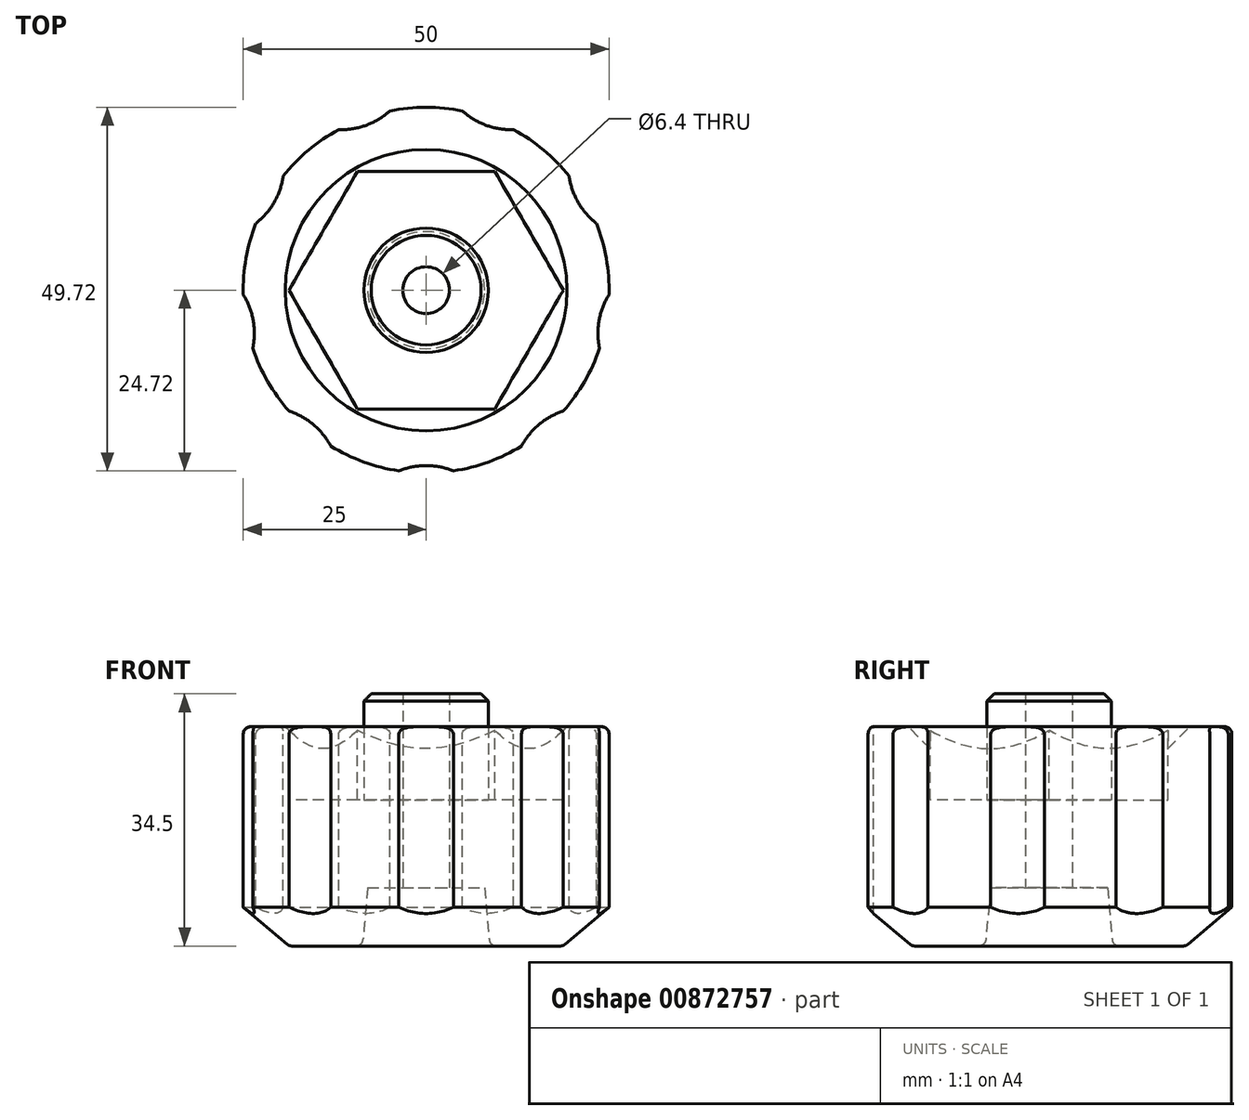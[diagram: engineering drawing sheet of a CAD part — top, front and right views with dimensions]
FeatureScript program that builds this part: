
annotation { "Feature Type Name" : "Feature", "Feature Type Description" : "" }
export const myFeature = defineFeature(function(context is Context, id is Id, definition is map)
    precondition{}
    {
        {
            var Q0;
            Q0=qCreatedBy(makeId("Front.planeOp"),FACE);
            var sketch = newSketch(context, id + "F0", { "sketchPlane" : qUnion([Q0])});
            skLineSegment(sketch, "E0", {"start": v(0, -6.14) * mm, "end": v(0, 36.57) * mm, "construction": true});
            skLineSegment(sketch, "E1", {"start": v(8.7, 0) * mm, "end": v(18.7, 0) * mm});
            skLineSegment(sketch, "E2", {"start": v(18.7, 0) * mm, "end": v(25, 5.29) * mm});
            skLineSegment(sketch, "E3", {"start": v(25, 5.29) * mm, "end": v(25, 30) * mm});
            skLineSegment(sketch, "E4", {"start": v(25, 30) * mm, "end": v(19.25, 30) * mm});
            skLineSegment(sketch, "E5", {"start": v(3.2, 34.5) * mm, "end": v(3.2, 8) * mm});
            skLineSegment(sketch, "E6", {"start": v(3.2, 8) * mm, "end": v(8, 8) * mm});
            skLineSegment(sketch, "E7", {"start": v(8, 8) * mm, "end": v(8.7, 0) * mm});
            skLineSegment(sketch, "E8", {"start": v(-29.63, 0) * mm, "end": v(44.02, 0) * mm, "construction": true});
            skLineSegment(sketch, "E9", {"start": v(19.25, 30) * mm, "end": v(16.25, 27) * mm});
            skLineSegment(sketch, "E10", {"start": v(16.25, 27) * mm, "end": v(16.25, 20) * mm});
            skLineSegment(sketch, "E11", {"start": v(16.25, 20) * mm, "end": v(8.5, 20) * mm});
            skLineSegment(sketch, "E12", {"start": v(8.5, 20) * mm, "end": v(8.5, 33.5) * mm});
            skLineSegment(sketch, "E13", {"start": v(8.5, 33.5) * mm, "end": v(7.5, 34.5) * mm});
            skLineSegment(sketch, "E14", {"start": v(7.5, 34.5) * mm, "end": v(3.2, 34.5) * mm});
            skSolve(sketch);
        }
        {
            var Q0;
            Q0=makeQuery(id+"F0.imprint","IMPRINT",FACE,{"disambiguationData":[TD([[makeQuery(id+"F0.imprint","IMPRINT",EDGE,{"derivedFrom":sQuery(id+"F0.wireOp",EDGE,"E1")}),1.0]])]});
            var Q1;
            Q1=sQuery(id+"F0.wireOp",EDGE,"E0");
            revolve(context, id + "F1", {"surfaceOperationType" : NewSurfaceOperationType.NEW, "entities" : qUnion([Q0]), "axis" : qUnion([Q1]), "revolveType" : RevolveType.FULL});
        }
        {
            var Q0;
            Q0=makeQuery(id+"F1.opRevolve","SWEPT_FACE",FACE,{"disambiguationData":[OSD([sQuery(id+"F0.wireOp",EDGE,"E4")])]});
            var sketch = newSketch(context, id + "F2", { "sketchPlane" : qUnion([Q0])});
            skLineSegment(sketch, "E15", {"start": v(0, 0) * mm, "end": v(0, 71.94) * mm, "construction": true});
            skLineSegment(sketch, "E16", {"start": v(0, 0) * mm, "end": v(26.2, 71.99) * mm, "construction": true});
            skCircle(sketch, "E17", {"center": v(11.63, 31.95) * mm, "radius": 10 * mm});
            skCircle(sketch, "E18.1.0", {"center": v(-11.63, 31.95) * mm, "radius": 10 * mm});
            skCircle(sketch, "E18.2.0", {"center": v(-29.44, 17) * mm, "radius": 10 * mm});
            skCircle(sketch, "E18.3.0", {"center": v(-33.48, -5.9) * mm, "radius": 10 * mm});
            skCircle(sketch, "E18.4.0", {"center": v(-21.85, -26.05) * mm, "radius": 10 * mm});
            skCircle(sketch, "E18.5.0", {"center": v(0, -34) * mm, "radius": 10 * mm});
            skCircle(sketch, "E18.6.0", {"center": v(21.85, -26.05) * mm, "radius": 10 * mm});
            skCircle(sketch, "E18.7.0", {"center": v(33.48, -5.9) * mm, "radius": 10 * mm});
            skCircle(sketch, "E18.8.0", {"center": v(29.44, 17) * mm, "radius": 10 * mm});
            skPoint(sketch, "E18.center", {"position": v(0, 0) * mm});
            skSolve(sketch);
        }
        {
            var Q0;
            Q0 = qSketchRegion(id + "F2", true);
            extrude(context, id + "F3", {"entities" : qUnion([Q0]), "operationType" : NewBodyOperationType.REMOVE, "endBound" : BoundingType.THROUGH_ALL, "oppositeDirection" : true, "depth" : 25 * mm, "offsetDistance" : 25 * mm});
        }
        {
            var Q0;
            Q0=makeQuery(id+"F1.opRevolve","SWEPT_EDGE",EDGE,{"disambiguationData":[OSD([sQuery(id+"F0.wireOp",EDGE,"E1"),sQuery(id+"F0.wireOp",EDGE,"E7")])]});
            var Q1;
            Q1=makeQuery(id+"F1.opRevolve","SWEPT_EDGE",EDGE,{"disambiguationData":[OSD([sQuery(id+"F0.wireOp",EDGE,"E1"),sQuery(id+"F0.wireOp",EDGE,"E2")])]});
            fillet(context, id + "F4", {"entities" : qUnion([Q0, Q1]), "tangentPropagation" : true, "radius" : 1 * mm, "defaultsChanged" : true, "vertexSettings" : [], "allowEdgeOverflow" : false});
        }
        {
            var Q0;
            Q0=makeQuery(id+"F3.boolean.opBoolean","COPY",EDGE,{"derivedFrom":makeQuery(id+"F3.opExtrude","CAP_EDGE",EDGE,{"disambiguationData":[OSD([sQuery(id+"F2.wireOp",EDGE,"E18.4.0")])],"isStart":true})});
            var Q1;
            {var subQ0=sQuery(id+"F0.wireOp",EDGE,"E3");var subQ1=sQuery(id+"F0.wireOp",EDGE,"E4");Q1=makeQuery(id+"F3.boolean.opBoolean","SPLIT",EDGE,{"disambiguationData":[TD([makeQuery(id+"F1.opRevolve","SWEPT_FACE",FACE,{"disambiguationData":[OSD([subQ0])]}),makeQuery(id+"F1.opRevolve","SWEPT_FACE",FACE,{"disambiguationData":[OSD([subQ1])]}),makeQuery(id+"F3.opExtrude","SWEPT_FACE",FACE,{"disambiguationData":[OSD([sQuery(id+"F2.wireOp",EDGE,"E18.4.0")])]}),makeQuery(id+"F3.opExtrude","SWEPT_FACE",FACE,{"disambiguationData":[OSD([sQuery(id+"F2.wireOp",EDGE,"E18.5.0")])]})])],"derivedFrom":makeQuery(id+"F1.opRevolve","SWEPT_EDGE",EDGE,{"disambiguationData":[OSD([subQ0,subQ1])]})});}
            var Q2;
            {var subQ0=sQuery(id+"F0.wireOp",EDGE,"E3");var subQ1=sQuery(id+"F0.wireOp",EDGE,"E4");Q2=makeQuery(id+"F3.boolean.opBoolean","SPLIT",EDGE,{"disambiguationData":[TD([makeQuery(id+"F1.opRevolve","SWEPT_FACE",FACE,{"disambiguationData":[OSD([subQ0])]}),makeQuery(id+"F1.opRevolve","SWEPT_FACE",FACE,{"disambiguationData":[OSD([subQ1])]}),makeQuery(id+"F3.opExtrude","SWEPT_FACE",FACE,{"disambiguationData":[OSD([sQuery(id+"F2.wireOp",EDGE,"E18.3.0")])]}),makeQuery(id+"F3.opExtrude","SWEPT_FACE",FACE,{"disambiguationData":[OSD([sQuery(id+"F2.wireOp",EDGE,"E18.4.0")])]})])],"derivedFrom":makeQuery(id+"F1.opRevolve","SWEPT_EDGE",EDGE,{"disambiguationData":[OSD([subQ0,subQ1])]})});}
            var Q3;
            Q3=makeQuery(id+"F3.boolean.opBoolean","COPY",EDGE,{"derivedFrom":makeQuery(id+"F3.opExtrude","CAP_EDGE",EDGE,{"disambiguationData":[OSD([sQuery(id+"F2.wireOp",EDGE,"E18.3.0")])],"isStart":true})});
            var Q4;
            {var subQ0=sQuery(id+"F0.wireOp",EDGE,"E3");var subQ1=sQuery(id+"F0.wireOp",EDGE,"E4");Q4=makeQuery(id+"F3.boolean.opBoolean","SPLIT",EDGE,{"disambiguationData":[TD([makeQuery(id+"F1.opRevolve","SWEPT_FACE",FACE,{"disambiguationData":[OSD([subQ0])]}),makeQuery(id+"F1.opRevolve","SWEPT_FACE",FACE,{"disambiguationData":[OSD([subQ1])]}),makeQuery(id+"F3.opExtrude","SWEPT_FACE",FACE,{"disambiguationData":[OSD([sQuery(id+"F2.wireOp",EDGE,"E18.2.0")])]}),makeQuery(id+"F3.opExtrude","SWEPT_FACE",FACE,{"disambiguationData":[OSD([sQuery(id+"F2.wireOp",EDGE,"E18.3.0")])]})])],"derivedFrom":makeQuery(id+"F1.opRevolve","SWEPT_EDGE",EDGE,{"disambiguationData":[OSD([subQ0,subQ1])]})});}
            var Q5;
            Q5=makeQuery(id+"F3.boolean.opBoolean","COPY",EDGE,{"derivedFrom":makeQuery(id+"F3.opExtrude","CAP_EDGE",EDGE,{"disambiguationData":[OSD([sQuery(id+"F2.wireOp",EDGE,"E18.2.0")])],"isStart":true})});
            var Q6;
            {var subQ0=sQuery(id+"F0.wireOp",EDGE,"E3");var subQ1=sQuery(id+"F0.wireOp",EDGE,"E4");Q6=makeQuery(id+"F3.boolean.opBoolean","SPLIT",EDGE,{"disambiguationData":[TD([makeQuery(id+"F1.opRevolve","SWEPT_FACE",FACE,{"disambiguationData":[OSD([subQ0])]}),makeQuery(id+"F1.opRevolve","SWEPT_FACE",FACE,{"disambiguationData":[OSD([subQ1])]}),makeQuery(id+"F3.opExtrude","SWEPT_FACE",FACE,{"disambiguationData":[OSD([sQuery(id+"F2.wireOp",EDGE,"E18.1.0")])]}),makeQuery(id+"F3.opExtrude","SWEPT_FACE",FACE,{"disambiguationData":[OSD([sQuery(id+"F2.wireOp",EDGE,"E18.2.0")])]})])],"derivedFrom":makeQuery(id+"F1.opRevolve","SWEPT_EDGE",EDGE,{"disambiguationData":[OSD([subQ0,subQ1])]})});}
            var Q7;
            Q7=makeQuery(id+"F3.boolean.opBoolean","COPY",EDGE,{"derivedFrom":makeQuery(id+"F3.opExtrude","CAP_EDGE",EDGE,{"disambiguationData":[OSD([sQuery(id+"F2.wireOp",EDGE,"E18.1.0")])],"isStart":true})});
            var Q8;
            {var subQ0=sQuery(id+"F0.wireOp",EDGE,"E3");var subQ1=sQuery(id+"F0.wireOp",EDGE,"E4");Q8=makeQuery(id+"F3.boolean.opBoolean","SPLIT",EDGE,{"disambiguationData":[TD([makeQuery(id+"F1.opRevolve","SWEPT_FACE",FACE,{"disambiguationData":[OSD([subQ0])]}),makeQuery(id+"F1.opRevolve","SWEPT_FACE",FACE,{"disambiguationData":[OSD([subQ1])]}),makeQuery(id+"F3.opExtrude","SWEPT_FACE",FACE,{"disambiguationData":[OSD([sQuery(id+"F2.wireOp",EDGE,"E17")])]}),makeQuery(id+"F3.opExtrude","SWEPT_FACE",FACE,{"disambiguationData":[OSD([sQuery(id+"F2.wireOp",EDGE,"E18.1.0")])]})])],"derivedFrom":makeQuery(id+"F1.opRevolve","SWEPT_EDGE",EDGE,{"disambiguationData":[OSD([subQ0,subQ1])]})});}
            var Q9;
            Q9=makeQuery(id+"F3.boolean.opBoolean","COPY",EDGE,{"derivedFrom":makeQuery(id+"F3.opExtrude","CAP_EDGE",EDGE,{"disambiguationData":[OSD([sQuery(id+"F2.wireOp",EDGE,"E17")])],"isStart":true})});
            var Q10;
            {var subQ0=sQuery(id+"F0.wireOp",EDGE,"E3");var subQ1=sQuery(id+"F0.wireOp",EDGE,"E4");Q10=makeQuery(id+"F3.boolean.opBoolean","SPLIT",EDGE,{"disambiguationData":[TD([makeQuery(id+"F1.opRevolve","SWEPT_FACE",FACE,{"disambiguationData":[OSD([subQ0])]}),makeQuery(id+"F1.opRevolve","SWEPT_FACE",FACE,{"disambiguationData":[OSD([subQ1])]}),makeQuery(id+"F3.opExtrude","SWEPT_FACE",FACE,{"disambiguationData":[OSD([sQuery(id+"F2.wireOp",EDGE,"E17")])]}),makeQuery(id+"F3.opExtrude","SWEPT_FACE",FACE,{"disambiguationData":[OSD([sQuery(id+"F2.wireOp",EDGE,"E18.8.0")])]})])],"derivedFrom":makeQuery(id+"F1.opRevolve","SWEPT_EDGE",EDGE,{"disambiguationData":[OSD([subQ0,subQ1])]})});}
            var Q11;
            Q11=makeQuery(id+"F3.boolean.opBoolean","COPY",EDGE,{"derivedFrom":makeQuery(id+"F3.opExtrude","CAP_EDGE",EDGE,{"disambiguationData":[OSD([sQuery(id+"F2.wireOp",EDGE,"E18.8.0")])],"isStart":true})});
            var Q12;
            {var subQ0=sQuery(id+"F0.wireOp",EDGE,"E3");var subQ1=sQuery(id+"F0.wireOp",EDGE,"E4");Q12=makeQuery(id+"F3.boolean.opBoolean","SPLIT",EDGE,{"disambiguationData":[TD([makeQuery(id+"F1.opRevolve","SWEPT_FACE",FACE,{"disambiguationData":[OSD([subQ0])]}),makeQuery(id+"F1.opRevolve","SWEPT_FACE",FACE,{"disambiguationData":[OSD([subQ1])]}),makeQuery(id+"F3.opExtrude","SWEPT_FACE",FACE,{"disambiguationData":[OSD([sQuery(id+"F2.wireOp",EDGE,"E18.7.0")])]}),makeQuery(id+"F3.opExtrude","SWEPT_FACE",FACE,{"disambiguationData":[OSD([sQuery(id+"F2.wireOp",EDGE,"E18.8.0")])]})])],"derivedFrom":makeQuery(id+"F1.opRevolve","SWEPT_EDGE",EDGE,{"disambiguationData":[OSD([subQ0,subQ1])]})});}
            var Q13;
            Q13=makeQuery(id+"F3.boolean.opBoolean","COPY",EDGE,{"derivedFrom":makeQuery(id+"F3.opExtrude","CAP_EDGE",EDGE,{"disambiguationData":[OSD([sQuery(id+"F2.wireOp",EDGE,"E18.7.0")])],"isStart":true})});
            var Q14;
            {var subQ0=sQuery(id+"F0.wireOp",EDGE,"E3");var subQ1=sQuery(id+"F0.wireOp",EDGE,"E4");Q14=makeQuery(id+"F3.boolean.opBoolean","SPLIT",EDGE,{"disambiguationData":[TD([makeQuery(id+"F1.opRevolve","SWEPT_FACE",FACE,{"disambiguationData":[OSD([subQ0])]}),makeQuery(id+"F1.opRevolve","SWEPT_FACE",FACE,{"disambiguationData":[OSD([subQ1])]}),makeQuery(id+"F3.opExtrude","SWEPT_FACE",FACE,{"disambiguationData":[OSD([sQuery(id+"F2.wireOp",EDGE,"E18.6.0")])]}),makeQuery(id+"F3.opExtrude","SWEPT_FACE",FACE,{"disambiguationData":[OSD([sQuery(id+"F2.wireOp",EDGE,"E18.7.0")])]})])],"derivedFrom":makeQuery(id+"F1.opRevolve","SWEPT_EDGE",EDGE,{"disambiguationData":[OSD([subQ0,subQ1])]})});}
            var Q15;
            Q15=makeQuery(id+"F3.boolean.opBoolean","COPY",EDGE,{"derivedFrom":makeQuery(id+"F3.opExtrude","CAP_EDGE",EDGE,{"disambiguationData":[OSD([sQuery(id+"F2.wireOp",EDGE,"E18.6.0")])],"isStart":true})});
            var Q16;
            {var subQ0=sQuery(id+"F0.wireOp",EDGE,"E3");var subQ1=sQuery(id+"F0.wireOp",EDGE,"E4");Q16=makeQuery(id+"F3.boolean.opBoolean","SPLIT",EDGE,{"disambiguationData":[TD([makeQuery(id+"F1.opRevolve","SWEPT_FACE",FACE,{"disambiguationData":[OSD([subQ0])]}),makeQuery(id+"F1.opRevolve","SWEPT_FACE",FACE,{"disambiguationData":[OSD([subQ1])]}),makeQuery(id+"F3.opExtrude","SWEPT_FACE",FACE,{"disambiguationData":[OSD([sQuery(id+"F2.wireOp",EDGE,"E18.5.0")])]}),makeQuery(id+"F3.opExtrude","SWEPT_FACE",FACE,{"disambiguationData":[OSD([sQuery(id+"F2.wireOp",EDGE,"E18.6.0")])]})])],"derivedFrom":makeQuery(id+"F1.opRevolve","SWEPT_EDGE",EDGE,{"disambiguationData":[OSD([subQ0,subQ1])]})});}
            var Q17;
            Q17=makeQuery(id+"F3.boolean.opBoolean","COPY",EDGE,{"derivedFrom":makeQuery(id+"F3.opExtrude","CAP_EDGE",EDGE,{"disambiguationData":[OSD([sQuery(id+"F2.wireOp",EDGE,"E18.5.0")])],"isStart":true})});
            fillet(context, id + "F5", {"entities" : qUnion([Q0, Q1, Q2, Q3, Q4, Q5, Q6, Q7, Q8, Q9, Q10, Q11, Q12, Q13, Q14, Q15, Q16, Q17]), "tangentPropagation" : true, "radius" : 1 * mm, "defaultsChanged" : false, "vertexSettings" : [], "allowEdgeOverflow" : false});
        }
        {
            var Q0;
            Q0=makeQuery(id+"F1.opRevolve","SWEPT_FACE",FACE,{"disambiguationData":[OSD([sQuery(id+"F0.wireOp",EDGE,"E4")])]});
            var sketch = newSketch(context, id + "F6", { "sketchPlane" : qUnion([Q0])});
            skCircle(sketch, "E19.cCircle", {"center": v(0, 0) * mm, "radius": 16.25 * mm, "construction": true});
            skLineSegment(sketch, "E19.0", {"start": v(-9.38, 16.25) * mm, "end": v(9.38, 16.25) * mm});
            skLineSegment(sketch, "E19.1", {"start": v(9.38, 16.25) * mm, "end": v(18.76, 0) * mm});
            skLineSegment(sketch, "E19.2", {"start": v(18.76, 0) * mm, "end": v(9.38, -16.25) * mm});
            skLineSegment(sketch, "E19.3", {"start": v(9.38, -16.25) * mm, "end": v(-9.38, -16.25) * mm});
            skLineSegment(sketch, "E19.4", {"start": v(-9.38, -16.25) * mm, "end": v(-18.76, 0) * mm});
            skLineSegment(sketch, "E19.5", {"start": v(-18.76, 0) * mm, "end": v(-9.38, 16.25) * mm});
            skPoint(sketch, "E19.0.midPoint", {"position": v(0, 16.25) * mm});
            skCircle(sketch, "E20", {"center": v(0, 0) * mm, "radius": 8.5 * mm});
            skSolve(sketch);
        }
        {
            var Q0;
            Q0 = qSketchRegion(id + "F6", true);
            var Q1;
            Q1=makeQuery(id+"F1.opRevolve","SWEPT_FACE",FACE,{"disambiguationData":[OSD([sQuery(id+"F0.wireOp",EDGE,"E11")])]});
            extrude(context, id + "F7", {"entities" : qUnion([Q0]), "operationType" : NewBodyOperationType.REMOVE, "endBound" : BoundingType.UP_TO_SURFACE, "oppositeDirection" : true, "depth" : 25 * mm, "endBoundEntityFace" : qUnion([Q1]), "offsetDistance" : 25 * mm});
        }
    });
